# Revit family: LAMP_LUP WALL 110 DIRECT INDIRECT
name_source: partatom
category: Luminarias
revit_build: Autodesk Revit 2018 (Build: 20190510_1515(x64)
units: mm (PartAtom-declared; Revit-internal decimal feet)

## family parameters
Anfitrión = Cara
Compartido = No
Corte con vacíos al cargar = No
Cota de conector redondo = Diámetro de uso
Origen de luz = Sí
Punto de cálculo de habitación = No
Tipo de pieza = Normal

## types (3) — shared parameters
CRI = 80
Cambio de temperatura de color de luz atenuada = <Ninguno>
Diameter = 110
Elevación por defecto = 1219 mm
Filtro de color = 16777215
Finish = Texturised black RAL 9011
Gear = Electronic
Height = 320
Installation instructions = https://www.lamp.es
Insulation class = I
Last update = 15/02/2022
MacAdam = 3
Manufacturer URL = http://www.lamp.es
Manufacturer country = Spain
Manufacturer name = LAMP
Material COB = LAMP_COB
Material cristal = LAMP_CRISTAL Aro Kombic
Material cuerpo = LAMP_Aluminio perfil Ocult NG
Material reflector = LAMP_Aluminio Reflector Imag
Power Supply = 220-240V 50/60Hz
Product URL = https://www.lamp.es
Product datasheet = http://www.lamp.es
Protection rating = IP65 / IK06
Ángulo de inclinación = 0.00°

## per-type parameters (varying)
| type | Archivo de red fotométrica | Efficacy | Indirect light | LED Lifetime | Lamp | Plum | Power | Product code | Type | Weight |
| 2510LM 4000 SPOT BLACK | LW1110DI40SP40NB_dir.IES | 68 lm/W | LAMP_LUP WALL 110 DIRECT INDIRECT_IND : 2510LM 4000 SPOT BLACK | 50.000 L70 | HIGH POWER LED | 37 W | 33 W | LW1110DI40SP40NB | HI POWER NICHIA | 2.70 kg |
| 2706LM 4000 FLOOD BLACK | LW1110DI40FL40NB_dir.IES | 88 lm/W | LAMP_LUP WALL 110 DIRECT INDIRECT_IND : 2706LM 4000 FLOOD BLACK | 50.000 L80 B10 | COB LED | 31 W | 27 W | LW1110DI40FL40NB | COB PHILIPS | 2.52 kg |
| 2748LM 4000 WIDE FLOOD BLACK | LW1110DI40WF40NB_dir.IES | 89 lm/W | LAMP_LUP WALL 110 DIRECT INDIRECT_IND : 2748LM 4000 WIDE FLOOD BLACK | 50.000 L80 B10 | COB LED | 31 W | 27 W | LW1110DI40WF40NB | COB PHILIPS | 2.52 kg |
